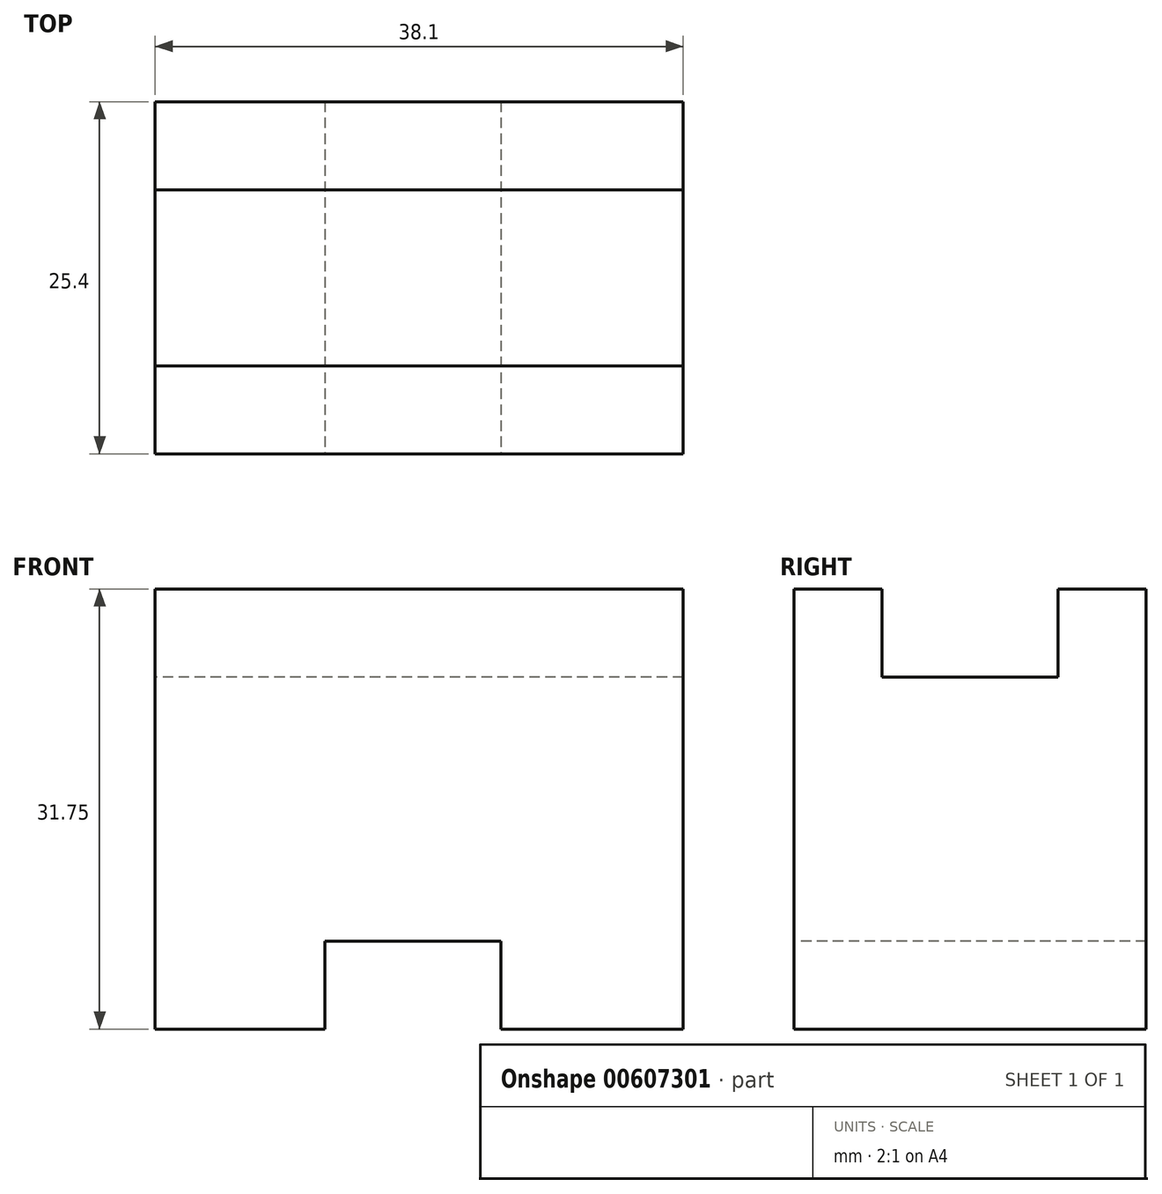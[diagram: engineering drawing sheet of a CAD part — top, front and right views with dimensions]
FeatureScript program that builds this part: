
annotation { "Feature Type Name" : "Feature", "Feature Type Description" : "" }
export const myFeature = defineFeature(function(context is Context, id is Id, definition is map)
    precondition{}
    {
        {
            var Q0;
            Q0=qCreatedBy(makeId("Right.planeOp"),FACE);
            var sketch = newSketch(context, id + "F0", { "sketchPlane" : qUnion([Q0])});
            skLineSegment(sketch, "E0", {"start": v(0, 0) * mm, "end": v(0, 31.75) * mm});
            skLineSegment(sketch, "E1", {"start": v(0, 31.75) * mm, "end": v(6.35, 31.75) * mm});
            skLineSegment(sketch, "E2", {"start": v(6.35, 31.75) * mm, "end": v(6.35, 25.4) * mm});
            skLineSegment(sketch, "E3", {"start": v(6.35, 25.4) * mm, "end": v(19.05, 25.4) * mm});
            skLineSegment(sketch, "E4", {"start": v(19.05, 25.4) * mm, "end": v(19.05, 31.75) * mm});
            skLineSegment(sketch, "E5", {"start": v(19.05, 31.75) * mm, "end": v(25.4, 31.75) * mm});
            skLineSegment(sketch, "E6", {"start": v(25.4, 31.75) * mm, "end": v(25.4, 0) * mm});
            skLineSegment(sketch, "E7", {"start": v(25.4, 0) * mm, "end": v(0, 0) * mm});
            skSolve(sketch);
        }
        {
            var Q0;
            Q0=makeQuery(id+"F0.imprint","IMPRINT",FACE,{"disambiguationData":[TD([[makeQuery(id+"F0.imprint","IMPRINT",EDGE,{"derivedFrom":sQuery(id+"F0.wireOp",EDGE,"E0")}),-1.0]])]});
            extrude(context, id + "F1", {"entities" : qUnion([Q0]), "depth" : 38.1 * mm, "offsetDistance" : 25.4 * mm});
        }
        {
            var Q0;
            Q0=qCreatedBy(makeId("Front.planeOp"),FACE);
            var sketch = newSketch(context, id + "F2", { "sketchPlane" : qUnion([Q0])});
            skLineSegment(sketch, "E8", {"start": v(12.25, 0) * mm, "end": v(12.25, 6.35) * mm});
            skLineSegment(sketch, "E9", {"start": v(12.25, 6.35) * mm, "end": v(24.95, 6.35) * mm});
            skLineSegment(sketch, "E10", {"start": v(24.95, 6.35) * mm, "end": v(24.95, 0) * mm});
            skLineSegment(sketch, "E11", {"start": v(24.95, 0) * mm, "end": v(12.25, 0) * mm});
            skSolve(sketch);
        }
        {
            var Q0;
            Q0=makeQuery(id+"F2.imprint","IMPRINT",FACE,{"disambiguationData":[TD([[makeQuery(id+"F2.imprint","IMPRINT",EDGE,{"derivedFrom":sQuery(id+"F2.wireOp",EDGE,"E8")}),-1.0]])]});
            extrude(context, id + "F3", {"entities" : qUnion([Q0]), "operationType" : NewBodyOperationType.REMOVE, "oppositeDirection" : true, "depth" : 25.4 * mm, "offsetDistance" : 25.4 * mm});
        }
    });
